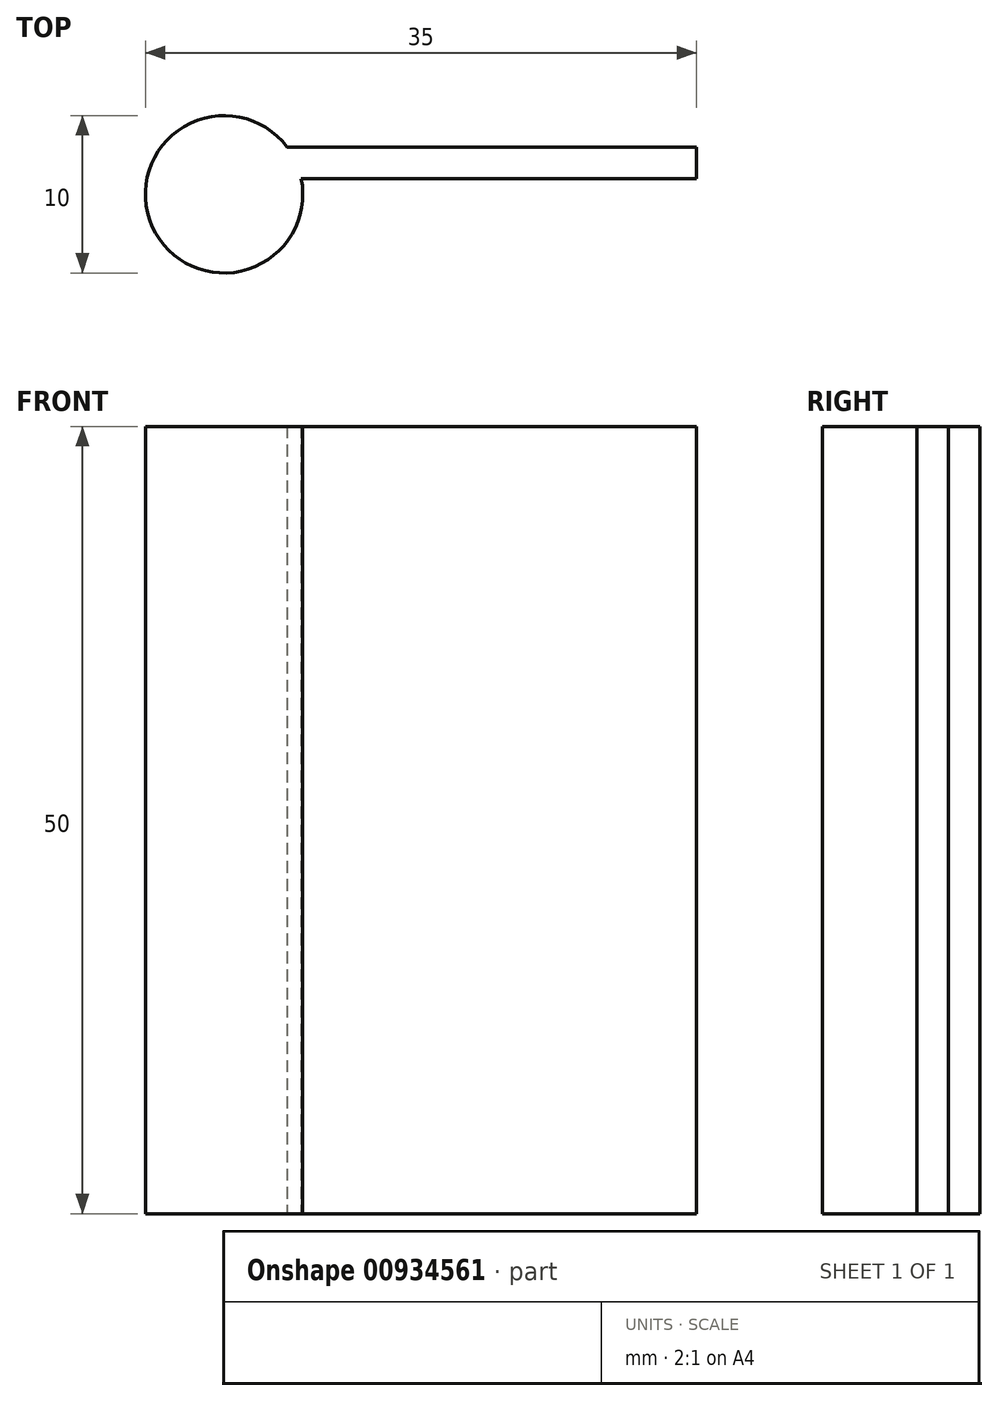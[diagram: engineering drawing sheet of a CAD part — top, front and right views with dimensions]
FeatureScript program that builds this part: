
annotation { "Feature Type Name" : "Feature", "Feature Type Description" : "" }
export const myFeature = defineFeature(function(context is Context, id is Id, definition is map)
    precondition{}
    {
        {
            var Q0;
            Q0=qCreatedBy(makeId("Top.planeOp"),FACE);
            var sketch = newSketch(context, id + "F0", { "sketchPlane" : qUnion([Q0])});
            skArc(sketch, "E0", {"start": v(4, -2) * mm, "mid": v(-4.56, -7.05) * mm, "end": v(4.9, -4) * mm});
            skLineSegment(sketch, "E1.bottom", {"start": v(4, -2) * mm, "end": v(30, -2) * mm});
            skLineSegment(sketch, "E1.top", {"start": v(4.9, -4) * mm, "end": v(30, -4) * mm});
            skLineSegment(sketch, "E1.right", {"start": v(30, -2) * mm, "end": v(30, -4) * mm});
            skPoint(sketch, "E1.left.start.orphan", {"position": v(0, -2) * mm});
            skSolve(sketch);
        }
        {
            var Q0;
            Q0 = qSketchRegion(id + "F0", true);
            extrude(context, id + "F1", {"entities" : qUnion([Q0]), "depth" : 50 * mm, "offsetDistance" : 25 * mm});
        }
    });
